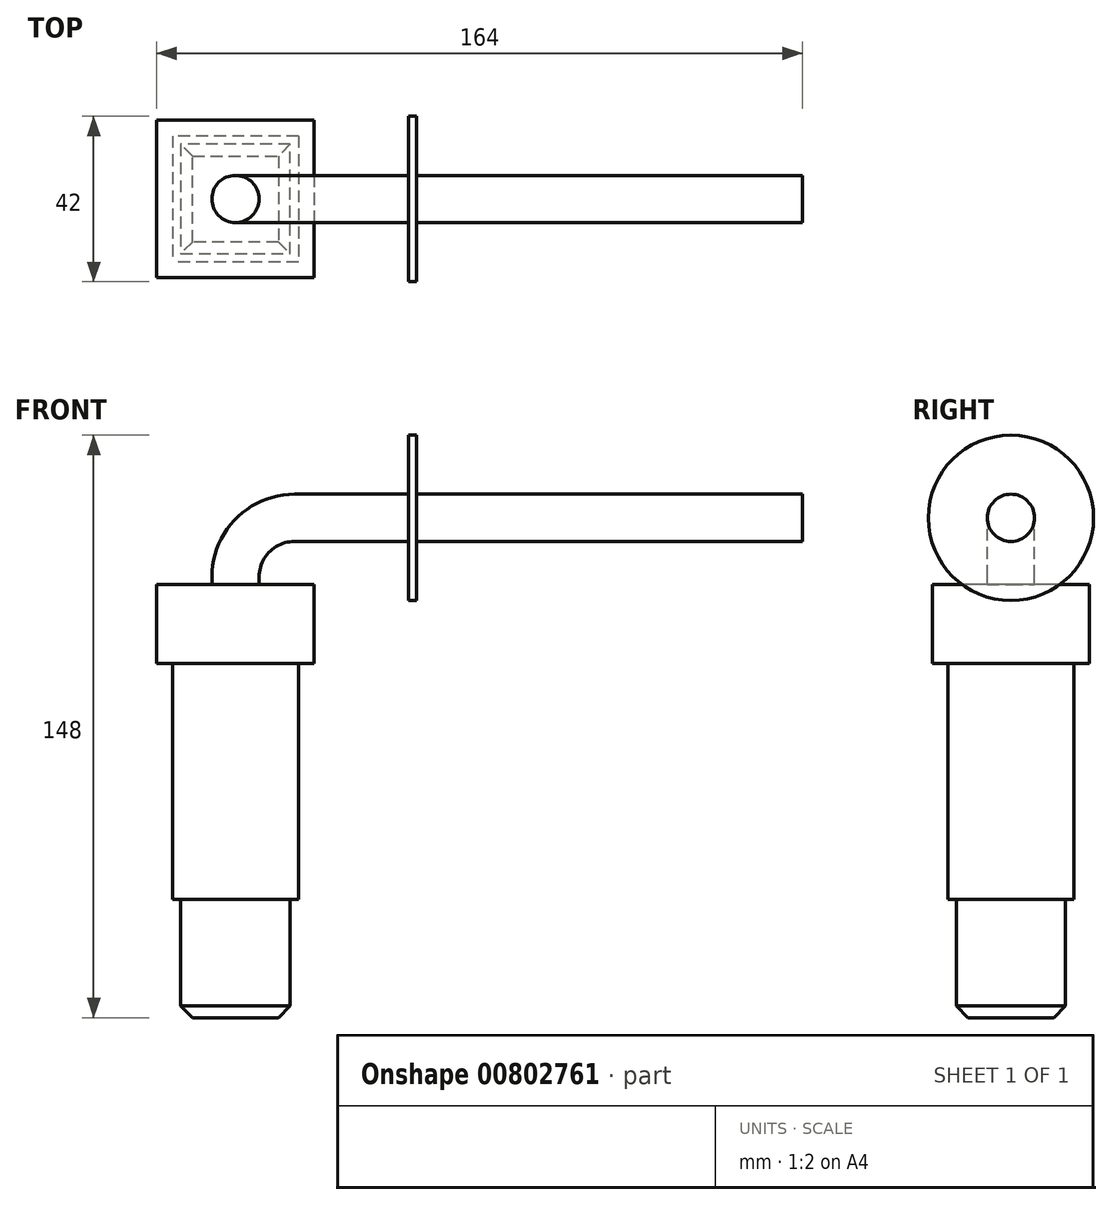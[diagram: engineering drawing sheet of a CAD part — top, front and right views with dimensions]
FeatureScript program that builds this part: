
annotation { "Feature Type Name" : "Feature", "Feature Type Description" : "" }
export const myFeature = defineFeature(function(context is Context, id is Id, definition is map)
    precondition{}
    {
        {
            var Q0;
            Q0=qCreatedBy(makeId("Top.planeOp"),FACE);
            var sketch = newSketch(context, id + "F0", { "sketchPlane" : qUnion([Q0])});
            skLineSegment(sketch, "E0.bottom", {"start": v(13.9, 13.9) * mm, "end": v(-13.9, 13.9) * mm});
            skLineSegment(sketch, "E0.top", {"start": v(13.9, -13.9) * mm, "end": v(-13.9, -13.9) * mm});
            skLineSegment(sketch, "E0.left", {"start": v(13.9, 13.9) * mm, "end": v(13.9, -13.9) * mm});
            skLineSegment(sketch, "E0.right", {"start": v(-13.9, 13.9) * mm, "end": v(-13.9, -13.9) * mm});
            skPoint(sketch, "E0.middle", {"position": v(0, 0) * mm});
            skSolve(sketch);
        }
        {
            var Q0;
            Q0=makeQuery(id+"F0.imprint","IMPRINT",FACE,{"disambiguationData":[TD([[makeQuery(id+"F0.imprint","IMPRINT",EDGE,{"derivedFrom":sQuery(id+"F0.wireOp",EDGE,"E0.bottom")}),1.0]])]});
            extrude(context, id + "F1", {"entities" : qUnion([Q0]), "depth" : 30 * mm, "offsetDistance" : 25 * mm});
        }
        {
            var Q0;
            Q0=makeQuery(id+"F1.opExtrude","CAP_FACE",FACE,{"disambiguationData":[OSD([sQuery(id+"F0.wireOp",EDGE,"E0.bottom"),sQuery(id+"F0.wireOp",EDGE,"E0.top"),sQuery(id+"F0.wireOp",EDGE,"E0.left"),sQuery(id+"F0.wireOp",EDGE,"E0.right")])],"isStart":false});
            var sketch = newSketch(context, id + "F2", { "sketchPlane" : qUnion([Q0])});
            skLineSegment(sketch, "E1.bottom", {"start": v(16, 16) * mm, "end": v(-16, 16) * mm});
            skLineSegment(sketch, "E1.top", {"start": v(16, -16) * mm, "end": v(-16, -16) * mm});
            skLineSegment(sketch, "E1.left", {"start": v(16, 16) * mm, "end": v(16, -16) * mm});
            skLineSegment(sketch, "E1.right", {"start": v(-16, 16) * mm, "end": v(-16, -16) * mm});
            skPoint(sketch, "E1.middle", {"position": v(0, 0) * mm});
            skSolve(sketch);
        }
        {
            var Q0;
            Q0=makeQuery(id+"F2.imprint","IMPRINT",FACE,{"disambiguationData":[TD([[makeQuery(id+"F2.imprint","IMPRINT",EDGE,{"derivedFrom":sQuery(id+"F2.wireOp",EDGE,"E1.bottom")}),1.0]])]});
            var Q1;
            Q1=makeQuery(id+"F2.imprint","IMPRINT",FACE,{"disambiguationData":[TD([[makeQuery(id+"F2.imprint","IMPRINT",EDGE,{"derivedFrom":makeQuery(id+"F1.opExtrude","CAP_EDGE",EDGE,{"disambiguationData":[OSD([sQuery(id+"F0.wireOp",EDGE,"E0.bottom")])],"isStart":false})}),1.0]])]});
            extrude(context, id + "F3", {"entities" : qUnion([Q0, Q1]), "operationType" : NewBodyOperationType.ADD, "depth" : 80 * mm, "offsetDistance" : 25 * mm});
        }
        {
            var Q0;
            Q0=makeQuery(id+"F3.opExtrude","CAP_FACE",FACE,{"disambiguationData":[OSD([sQuery(id+"F2.wireOp",EDGE,"E1.bottom"),sQuery(id+"F2.wireOp",EDGE,"E1.top"),sQuery(id+"F2.wireOp",EDGE,"E1.left"),sQuery(id+"F2.wireOp",EDGE,"E1.right")])],"isStart":false});
            var sketch = newSketch(context, id + "F4", { "sketchPlane" : qUnion([Q0])});
            skLineSegment(sketch, "E2.bottom", {"start": v(20, 20) * mm, "end": v(-20, 20) * mm});
            skLineSegment(sketch, "E2.top", {"start": v(20, -20) * mm, "end": v(-20, -20) * mm});
            skLineSegment(sketch, "E2.left", {"start": v(20, 20) * mm, "end": v(20, -20) * mm});
            skLineSegment(sketch, "E2.right", {"start": v(-20, 20) * mm, "end": v(-20, -20) * mm});
            skPoint(sketch, "E2.middle", {"position": v(0, 0) * mm});
            skSolve(sketch);
        }
        {
            var Q0;
            Q0 = qSketchRegion(id + "F4", true);
            extrude(context, id + "F5", {"entities" : qUnion([Q0]), "operationType" : NewBodyOperationType.ADD, "oppositeDirection" : true, "depth" : 20 * mm, "offsetDistance" : 25 * mm});
        }
        {
            var Q0;
            Q0=qCreatedBy(makeId("Front.planeOp"),FACE);
            var sketch = newSketch(context, id + "F6", { "sketchPlane" : qUnion([Q0])});
            skLineSegment(sketch, "E3", {"start": v(0, 110) * mm, "end": v(0, 112) * mm});
            skLineSegment(sketch, "E4", {"start": v(15, 127) * mm, "end": v(144, 127) * mm});
            skPoint(sketch, "E5.visualSharp", {"position": v(0, 127) * mm});
            skArc(sketch, "E5.filletArc", {"start": v(15, 127) * mm, "mid": v(4.4, 122.6) * mm, "end": v(0, 112) * mm});
            skSolve(sketch);
        }
        {
            var Q0;
            Q0=makeQuery(id+"F5.boolean.opBoolean","MERGE",FACE,{"derivedFrom":[makeQuery(id+"F3.opExtrude","CAP_FACE",FACE,{"disambiguationData":[OSD([sQuery(id+"F2.wireOp",EDGE,"E1.bottom"),sQuery(id+"F2.wireOp",EDGE,"E1.top"),sQuery(id+"F2.wireOp",EDGE,"E1.left"),sQuery(id+"F2.wireOp",EDGE,"E1.right")])],"isStart":false}),makeQuery(id+"F5.opExtrude","CAP_FACE",FACE,{"disambiguationData":[OSD([sQuery(id+"F4.wireOp",EDGE,"E2.bottom"),sQuery(id+"F4.wireOp",EDGE,"E2.top"),sQuery(id+"F4.wireOp",EDGE,"E2.left"),sQuery(id+"F4.wireOp",EDGE,"E2.right")])],"isStart":true})]});
            var sketch = newSketch(context, id + "F7", { "sketchPlane" : qUnion([Q0])});
            skCircle(sketch, "E6", {"center": v(0, 0) * mm, "radius": 6 * mm});
            skSolve(sketch);
        }
        {
            var Q0;
            Q0=makeQuery(id+"F7.imprint","IMPRINT",FACE,{"disambiguationData":[TD([[makeQuery(id+"F7.imprint","IMPRINT",EDGE,{"derivedFrom":sQuery(id+"F7.wireOp",EDGE,"E6")}),1.0]])]});
            var Q1;
            Q1=sQuery(id+"F6.wireOp",EDGE,"E3");
            var Q2;
            Q2=sQuery(id+"F6.wireOp",EDGE,"E5.filletArc");
            var Q3;
            Q3=sQuery(id+"F6.wireOp",EDGE,"E4");
            sweep(context, id + "F8", {"operationType" : NewBodyOperationType.ADD, "profiles" : qUnion([Q0]), "path" : qUnion([Q1, Q2, Q3])});
        }
        {
            var Q0;
            Q0=makeQuery(id+"F8.opSweep","CAP_FACE",FACE,{"disambiguationData":[OSD([sQuery(id+"F6.wireOp",VERTEX,"E4.end"),sQuery(id+"F7.wireOp",EDGE,"E6")])],"isStart":false});
            cPlane(context, id + "F9", {"entities" : qUnion([Q0]), "cplaneType" : CPlaneType.OFFSET, "offset" : 100 * mm, "oppositeDirection" : true, "width" : 150 * mm, "height" : 150 * mm});
        }
        {
            var Q0;
            Q0=qCreatedBy(id+"F9.planeOp",FACE);
            var sketch = newSketch(context, id + "F10", { "sketchPlane" : qUnion([Q0])});
            skCircle(sketch, "E7", {"center": v(0, 127) * mm, "radius": 21 * mm});
            skSolve(sketch);
        }
        {
            var Q0;
            Q0=makeQuery(id+"F10.imprint","IMPRINT",FACE,{"disambiguationData":[TD([[makeQuery(id+"F10.imprint","IMPRINT",EDGE,{"derivedFrom":sQuery(id+"F10.wireOp",EDGE,"E7")}),1.0]])]});
            extrude(context, id + "F11", {"entities" : qUnion([Q0]), "operationType" : NewBodyOperationType.ADD, "depth" : 2 * mm, "offsetDistance" : 25 * mm});
        }
        {
            var Q0;
            Q0=makeQuery(id+"F1.opExtrude","CAP_EDGE",EDGE,{"disambiguationData":[OSD([sQuery(id+"F0.wireOp",EDGE,"E0.top")])],"isStart":true});
            var Q1;
            Q1=makeQuery(id+"F1.opExtrude","CAP_EDGE",EDGE,{"disambiguationData":[OSD([sQuery(id+"F0.wireOp",EDGE,"E0.left")])],"isStart":true});
            var Q2;
            Q2=makeQuery(id+"F1.opExtrude","CAP_EDGE",EDGE,{"disambiguationData":[OSD([sQuery(id+"F0.wireOp",EDGE,"E0.bottom")])],"isStart":true});
            var Q3;
            Q3=makeQuery(id+"F1.opExtrude","CAP_EDGE",EDGE,{"disambiguationData":[OSD([sQuery(id+"F0.wireOp",EDGE,"E0.right")])],"isStart":true});
            chamfer(context, id + "F12", {"entities" : qUnion([Q0, Q1, Q2, Q3]), "width" : 3 * mm, "tangentPropagation" : true});
        }
    });
